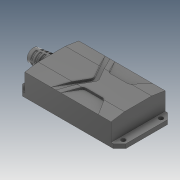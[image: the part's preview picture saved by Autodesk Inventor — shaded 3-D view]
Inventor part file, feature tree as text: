
AUTODESK INVENTOR PART (.ipt)
format: ipt  version: 2020 (Build 240168000, 168)  size: 336,384 bytes
history: native  units: mm
features: sketch x12, extrude x10, plane x8, chamfer x1, fillet x1, loft x1
ambient origin geometry x8: Origin, YZ Plane, XZ Plane, XY Plane, X Axis, Y Axis, Z Axis, Center Point
bodies: Solid1 (feature_tree)
feature tree (33):
  extrude  "Extrusion1"  Depth=25.8mm
  chamfer  "Chamfer1"  Distance=2.0mm
  extrude  "Extrusion2"  Depth=2.0mm
  plane  "Work Plane1"
  extrude  "Extrusion3"  Depth=18.0mm
  extrude  "Extrusion4"  Depth=11.5mm
  fillet  "Fillet1"  Radius=13.0mm
  sketch  "Sketch6"  dims[d14=10.5mm d15=41.2mm d16=0.0mm]
  plane  "Work Plane2"
  loft  "Loft1"
  plane  "Work Plane3"
  extrude  "Extrusion5"  Depth=2.0mm
  plane  "Work Plane4"
  extrude  "Extrusion6"  Depth=20.0mm
  plane  "Work Plane5"
  extrude  "Extrusion7"  Depth=7.0mm
  plane  "Work Plane6"
  extrude  "Extrusion8"  Depth=1.0mm TaperAngle=0.0deg
  plane  "Work Plane7"
  extrude  "Extrusion9"  Depth=8.0mm
  plane  "Work Plane8"
  extrude  "Extrusion10"  Depth=8.8mm
  sketch  "Sketch1"  dims[d0=49.4mm d1=25.8mm d2=2.0mm d3=0.0mm]
  sketch  "Sketch2"  dims[d4=3.0mm d5=2.0mm d6=45.0deg d7=2.0mm]
  sketch  "Sketch3"  dims[d8=45.2mm d9=18.0mm]
  sketch  "Sketch4"  dims[d10=2.0mm d11=0.0mm d12=11.5mm d13=13.0mm]
  sketch  "Sketch7"  dims[d17=2.0mm d18=2.0mm]
  sketch  "Sketch8"  dims[d19=120.0deg d20=20.0mm]
  sketch  "Sketch9"  dims[d21=2.0mm d22=7.0mm]
  sketch  "Sketch10"  dims[d23=18.0mm d24=1.0mm d25=0.0mm]
  sketch  "Sketch11"  dims[d26=2.0mm d27=8.0mm]
  sketch  "Sketch12"  dims[d28=4.75mm d29=8.8mm]
  sketch  "Sketch13"  dims[d30=6.0mm d31=0.0mm d32=90.0deg d33=0.0mm d34=90.0deg d35=1.0mm d36=6.776mm d37=1.0mm d38=1.0mm d39=1.0mm d40=0.0mm d41=1.0mm d42=6.577mm d43=1.0mm d44=1.0mm d45=8.0mm d46=1.0mm d47=0.0mm d48=1.0mm d49=6.338mm d50=1.0mm d51=1.0mm d52=1.0mm d53=0.0mm d54=1.0mm d55=6.061mm d56=1.0mm d57=1.0mm d58=1.0mm d59=0.0mm d60=1.0mm d61=5.871mm d62=1.0mm d63=1.0mm d64=1.0mm d65=0.0mm d66=1.0mm d67=5.548mm d68=1.0mm d69=1.0mm d70=1.0mm d71=0.0mm]
